FCSTD DOCUMENT  (FreeCAD 1.0R39109 (Git))
Label: Cinematic
License: All rights reserved
LicenseURL: https://en.wikipedia.org/wiki/All_rights_reserved
objects: App::DocumentObjectGroup×3, PartDesign::CoordinateSystem×1, App::FeaturePython×1, Sketcher::SketchObject×1, App::Part×1
note: 3 computed .brp shape members not serialized (recipe doc carries the construction recipe); baked Part::Feature solids carry a one-line shape summary decoded from their .brp

FEATURE [App::DocumentObjectGroup] Parts
FEATURE [PartDesign::CoordinateSystem] LCS_Origin
  AttacherType = Attacher::AttachEngine3D
  AttachmentSupport = -> [X_Axis]
  MapMode = 2
FEATURE [App::DocumentObjectGroup] Constraints
FEATURE [App::FeaturePython] Variables  # WARN: FeaturePython — macro-defined, semantics opaque (R4)
  E = 50
  G1 = 30
  H1 = 48
  O5_Angle = 98
  O7_Angle = 100
  Type = App::PropertyContainer
  b = 20
  c = 70
  d = 60
  f = 25
  i = 35
FEATURE [App::DocumentObjectGroup] Configurations
FEATURE [Sketcher::SketchObject] Sketch_1
  ArcFitTolerance = 1e-06
  AttachmentSupport = -> [LCS_Origin]
  FullyConstrained = true
  MakeInternals = false
  MapMode = 5
  expr: Constraints[10] = Variables.b
  expr: Constraints[11] = Variables.c
  expr: Constraints[12] = Variables.i
  expr: Constraints[13] = Variables.G1
  expr: Constraints[19] = Variables.O7_Angle
  expr: Constraints[9] = Variables.E
  sketch-geometry (11):
    g0: LineSegment StartX=0 StartY=0 StartZ=0 EndX=28.1148 EndY=41.3468 EndZ=0
    g1: LineSegment StartX=28.1148 StartY=41.3468 StartZ=0 EndX=8.51809 EndY=64.0617 EndZ=0
    g2: LineSegment StartX=8.51809 StartY=64.0617 StartZ=0 EndX=42.2601 EndY=73.361 EndZ=0
    g3: LineSegment StartX=53.0015 StartY=45.7258 StartZ=0 EndX=44.9646 EndY=-23.8114 EndZ=0
    g4: LineSegment StartX=44.9646 StartY=-23.8114 StartZ=0 EndX=25 EndY=-25 EndZ=0
    g5: LineSegment StartX=28.1148 StartY=41.3468 StartZ=0 EndX=53.0015 EndY=45.7258 EndZ=0
    g6: LineSegment StartX=53.0015 StartY=45.7258 StartZ=0 EndX=0 EndY=0 EndZ=0
    g7: LineSegment StartX=8.51809 StartY=64.0617 StartZ=0 EndX=-11.0787 EndY=86.7766 EndZ=0
    g8: LineSegment StartX=-11.0787 StartY=86.7766 StartZ=0 EndX=42.2601 EndY=73.361 EndZ=0
    g9: LineSegment StartX=53.0015 StartY=45.7258 StartZ=0 EndX=60.5731 EndY=52.258 EndZ=0
    g10: LineSegment StartX=53.0015 StartY=45.7258 StartZ=0 EndX=34.8875 EndY=92.3292 EndZ=0
  constraints (31):
    c: Coincident(g-1,g0)
    c: Coincident(g0,g1)
    c: Coincident(g1,g2)
    c: Coincident(g3,g4)
    c: Coincident(g0,g5)
    c: Coincident(g5,g6)
    c: Coincident(g6,g0)
    c: DistanceX(g4) = 25
    c: DistanceY(g4) = -25
    c: Distance(g0,g0) = 50
    c: Distance(g4,g4) = 20
    c: Distance(g3,g3) = 70
    c: Distance(g2,g2) = 35
    c: Distance(g1,g1) = 30
    c: Angle(g6,g0) = 0.261799
    c: Coincident(g1,g7)
    c: Coincident(g7,g8)
    c: Coincident(g8,g2)
    c: Distance(g7,g7) = 30
    c: Angle(g3,g4) = 1.74533
    c: Angle(g6,g9) = 3.14159
    c: Distance(g0,g9) = 80
    c: Distance(g8,g8) = 55
    c: Distance(g6,g6) = 70
    c: Coincident(g10,g3)
    c: PointOnObject(g2,g10)
    c: Coincident(g9,g3)
    c: Coincident(g3,g5)
    c: Distance(g10,g10) = 50
    c: Angle(g1,g0) = 1.8326
    c: Angle(g7,g1) = 3.14159
FEATURE [App::Part] Assembly
  AssemblyType = Part::Link
  Group = -> [LCS_Origin,Constraints,Variables,Configurations,Sketch_1]
  Origin = -> Origin
  Type = Assembly
